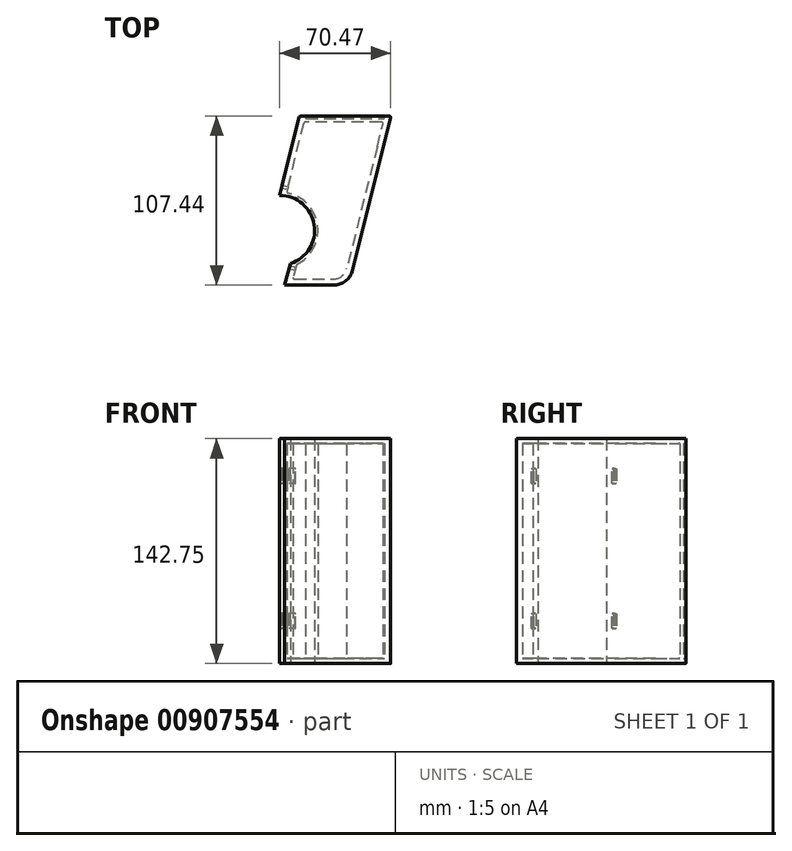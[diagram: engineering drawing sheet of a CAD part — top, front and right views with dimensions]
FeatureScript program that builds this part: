
annotation { "Feature Type Name" : "Feature", "Feature Type Description" : "" }
export const myFeature = defineFeature(function(context is Context, id is Id, definition is map)
    precondition{}
    {
        {
            var Q0;
            Q0=qCreatedBy(makeId("Top.planeOp"),FACE);
            var sketch = newSketch(context, id + "F0", { "sketchPlane" : qUnion([Q0])});
            skArc(sketch, "E0", {"start": v(6.82, -21.15) * mm, "mid": v(21.96, 3.45) * mm, "end": v(0, 22.23) * mm});
            skLineSegment(sketch, "E1", {"start": v(0, 22.22) * mm, "end": v(1.58, 28.53) * mm});
            skLineSegment(sketch, "E2.trimOffspring", {"start": v(6.82, -21.15) * mm, "end": v(3.22, -34.85) * mm});
            skLineSegment(sketch, "E3", {"start": v(3.22, -34.85) * mm, "end": v(16.42, -34.85) * mm});
            skPoint(sketch, "E4.orphan", {"position": v(0, -47.1) * mm});
            skPoint(sketch, "E5.visualSharp", {"position": v(36.5, -34.85) * mm});
            skPoint(sketch, "E6.newPointB", {"position": v(49.9, -44.72) * mm});
            skLineSegment(sketch, "E7", {"start": v(3.22, -34.85) * mm, "end": v(0.71, -44.38) * mm});
            skLineSegment(sketch, "E8", {"start": v(0.71, -44.38) * mm, "end": v(16.4, -44.38) * mm});
            skLineSegment(sketch, "E9.0", {"start": v(66.86, 57.06) * mm, "end": v(48.28, -17.24) * mm});
            skLineSegment(sketch, "E10", {"start": v(16.42, -34.85) * mm, "end": v(33.97, -34.85) * mm});
            skLineSegment(sketch, "E11", {"start": v(1.58, 28.53) * mm, "end": v(8.82, 57.52) * mm});
            skArc(sketch, "E12.filletArc", {"start": v(33.97, -34.85) * mm, "mid": v(41.73, -32.2) * mm, "end": v(46.26, -25.35) * mm});
            skLineSegment(sketch, "E13", {"start": v(48.28, -17.24) * mm, "end": v(46.26, -25.35) * mm});
            skLineSegment(sketch, "E14.0", {"start": v(9.88, -24.5) * mm, "end": v(8.48, -29.83) * mm});
            skLineSegment(sketch, "E14.1", {"start": v(9.41, -31.04) * mm, "end": v(16.73, -31.04) * mm});
            skLineSegment(sketch, "E14.2", {"start": v(16.73, -31.04) * mm, "end": v(33.97, -31.04) * mm});
            skArc(sketch, "E14.3", {"start": v(33.97, -31.04) * mm, "mid": v(39.4, -29.19) * mm, "end": v(42.56, -24.4) * mm});
            skLineSegment(sketch, "E14.4", {"start": v(44.59, -16.31) * mm, "end": v(42.56, -24.4) * mm});
            skLineSegment(sketch, "E14.6", {"start": v(5.01, 26.57) * mm, "end": v(5.27, 27.6) * mm});
            skLineSegment(sketch, "E14.7", {"start": v(5.27, 27.6) * mm, "end": v(11.8, 53.7) * mm});
            skLineSegment(sketch, "E14.10", {"start": v(61.97, 53.23) * mm, "end": v(44.59, -16.31) * mm});
            skPoint(sketch, "E15.visualSharp", {"position": v(4.77, 25.6) * mm});
            skPoint(sketch, "E16.visualSharp", {"position": v(8.16, -31.04) * mm});
            skArc(sketch, "E16.filletArc", {"start": v(8.48, -29.83) * mm, "mid": v(8.65, -30.66) * mm, "end": v(9.41, -31.04) * mm});
            skPoint(sketch, "E17.visualSharp", {"position": v(10, -24.04) * mm});
            skArc(sketch, "E18.0", {"start": v(10.68, -21.78) * mm, "mid": v(24.09, 2.85) * mm, "end": v(5.3, 23.67) * mm});
            skLineSegment(sketch, "E19", {"start": v(9.88, -24.5) * mm, "end": v(10.55, -21.93) * mm});
            skArc(sketch, "E20.filletArc", {"start": v(10.68, -21.78) * mm, "mid": v(10.6, -21.84) * mm, "end": v(10.55, -21.93) * mm});
            skLineSegment(sketch, "E21", {"start": v(5.01, 26.57) * mm, "end": v(4.58, 24.85) * mm});
            skArc(sketch, "E22.filletArc", {"start": v(4.58, 24.85) * mm, "mid": v(4.7, 24.1) * mm, "end": v(5.3, 23.67) * mm});
            skLineSegment(sketch, "E23.0", {"start": v(16.3, 72.6) * mm, "end": v(13.35, 72.6) * mm});
            skLineSegment(sketch, "E24", {"start": v(66.86, 57.06) * mm, "end": v(70.44, 71.4) * mm});
            skLineSegment(sketch, "E25", {"start": v(8.82, 57.52) * mm, "end": v(12.4, 71.86) * mm});
            skLineSegment(sketch, "E26", {"start": v(66.66, 72.6) * mm, "end": v(69.5, 72.6) * mm});
            skArc(sketch, "E27.filletArc", {"start": v(70.44, 71.4) * mm, "mid": v(70.27, 72.22) * mm, "end": v(69.5, 72.6) * mm});
            skArc(sketch, "E28.filletArc", {"start": v(13.35, 72.6) * mm, "mid": v(12.75, 72.4) * mm, "end": v(12.4, 71.86) * mm});
            skLineSegment(sketch, "E29.0", {"start": v(63, 71.07) * mm, "end": v(16.75, 71.07) * mm});
            skLineSegment(sketch, "E30.0", {"start": v(63, 68.78) * mm, "end": v(16.32, 68.78) * mm});
            skLineSegment(sketch, "E31", {"start": v(11.8, 53.7) * mm, "end": v(15.38, 68.05) * mm});
            skLineSegment(sketch, "E32", {"start": v(61.97, 53.23) * mm, "end": v(65.56, 67.59) * mm});
            skArc(sketch, "E33.filletArc", {"start": v(16.32, 68.78) * mm, "mid": v(15.73, 68.58) * mm, "end": v(15.38, 68.05) * mm});
            skLineSegment(sketch, "E34", {"start": v(63, 68.78) * mm, "end": v(64.63, 68.78) * mm});
            skLineSegment(sketch, "E35", {"start": v(16.52, 72.37) * mm, "end": v(16.52, 71.3) * mm});
            skLineSegment(sketch, "E36", {"start": v(63, 71.07) * mm, "end": v(66.2, 71.07) * mm});
            skLineSegment(sketch, "E37", {"start": v(66.43, 71.3) * mm, "end": v(66.43, 72.37) * mm});
            skPoint(sketch, "E38.newPointA", {"position": v(66.43, 72.6) * mm});
            skArc(sketch, "E38.filletArc", {"start": v(66.66, 72.6) * mm, "mid": v(66.5, 72.53) * mm, "end": v(66.43, 72.37) * mm});
            skPoint(sketch, "E39.visualSharp", {"position": v(66.43, 71.07) * mm});
            skArc(sketch, "E39.filletArc", {"start": v(66.2, 71.07) * mm, "mid": v(66.37, 71.14) * mm, "end": v(66.43, 71.3) * mm});
            skArc(sketch, "E40.filletArc", {"start": v(16.52, 71.3) * mm, "mid": v(16.59, 71.14) * mm, "end": v(16.75, 71.07) * mm});
            skArc(sketch, "E41.filletArc", {"start": v(16.52, 72.37) * mm, "mid": v(16.45, 72.53) * mm, "end": v(16.3, 72.6) * mm});
            skPoint(sketch, "E42.visualSharp", {"position": v(65.86, 68.78) * mm});
            skArc(sketch, "E42.filletArc", {"start": v(65.56, 67.59) * mm, "mid": v(65.39, 68.41) * mm, "end": v(64.63, 68.78) * mm});
            skSolve(sketch);
        }
        {
            var Q0;
            Q0=makeQuery(id+"F0.imprint","IMPRINT",FACE,{"disambiguationData":[TD([[makeQuery(id+"F0.imprint","IMPRINT",EDGE,{"derivedFrom":sQuery(id+"F0.wireOp",EDGE,"E0")}),-1.0]])]});
            extrude(context, id + "F1", {"entities" : qUnion([Q0]), "depth" : 6.35 * mm, "offsetDistance" : 25.4 * mm});
        }
        {
            var Q0;
            Q0 = qSketchRegion(id + "F0", true);
            var Q1;
            Q1=makeQuery(id+"F1.opExtrude","CAP_FACE",FACE,{"disambiguationData":[OSD([sQuery(id+"F0.wireOp",EDGE,"E0"),sQuery(id+"F0.wireOp",EDGE,"E1"),sQuery(id+"F0.wireOp",EDGE,"E2.trimOffspring"),sQuery(id+"F0.wireOp",EDGE,"E3"),sQuery(id+"F0.wireOp",EDGE,"E9.0"),sQuery(id+"F0.wireOp",EDGE,"E10"),sQuery(id+"F0.wireOp",EDGE,"E11"),sQuery(id+"F0.wireOp",EDGE,"UJC1U5ST-MCEr-nF2W-ny8S-TELihmCuxkUr"),sQuery(id+"F0.wireOp",EDGE,"e7e2a3fe-8400-48dc-a1a8-9a47f7191577.filletArc"),sQuery(id+"F0.wireOp",EDGE,"f4f465a5-f153-4e84-8156-ec9705fb6cea.filletArc"),sQuery(id+"F0.wireOp",EDGE,"E12.filletArc"),sQuery(id+"F0.wireOp",EDGE,"E13"),sQuery(id+"F0.wireOp",EDGE,"E14.0"),sQuery(id+"F0.wireOp",EDGE,"E14.1"),sQuery(id+"F0.wireOp",EDGE,"E14.2"),sQuery(id+"F0.wireOp",EDGE,"E14.3"),sQuery(id+"F0.wireOp",EDGE,"E14.4"),sQuery(id+"F0.wireOp",EDGE,"E14.5"),sQuery(id+"F0.wireOp",EDGE,"E14.6"),sQuery(id+"F0.wireOp",EDGE,"E14.7"),sQuery(id+"F0.wireOp",EDGE,"E14.8"),sQuery(id+"F0.wireOp",EDGE,"E14.10"),sQuery(id+"F0.wireOp",EDGE,"57333c07-2634-475e-aa19-e25420147b81.filletArc"),sQuery(id+"F0.wireOp",EDGE,"e2d5d6c9-fdbc-41b1-8945-850c04fe5a9c.filletArc"),sQuery(id+"F0.wireOp",EDGE,"E15.filletArc"),sQuery(id+"F0.wireOp",EDGE,"E16.filletArc"),sQuery(id+"F0.wireOp",EDGE,"E17.filletArc")])],"isStart":false});
            extrude(context, id + "F2", {"entities" : qUnion([Q0, Q1]), "operationType" : NewBodyOperationType.ADD, "depth" : 133.35 * mm, "offsetDistance" : 25.4 * mm});
        }
        {
            var Q0;
            {var subQ0=sQuery(id+"F0.wireOp",EDGE,"E2.trimOffspring");Q0=makeQuery(id+"F2.boolean.opBoolean","MERGE",FACE,{"derivedFrom":[makeQuery(id+"F1.opExtrude","SWEPT_FACE",FACE,{"disambiguationData":[OSD([subQ0])]}),makeQuery(id+"F2.opExtrude","SWEPT_FACE",FACE,{"disambiguationData":[OSD([subQ0]),TDD([makeQuery(id+"F0.imprint","IMPRINT",EDGE,{"derivedFrom":subQ0})])]}),makeQuery(id+"F2.opExtrude","SWEPT_FACE",FACE,{"disambiguationData":[OSD([subQ0]),TDD([makeQuery(id+"F1.opExtrude","CAP_EDGE",EDGE,{"disambiguationData":[OSD([subQ0])],"isStart":false})])]})]});}
            var sketch = newSketch(context, id + "F3", { "sketchPlane" : qUnion([Q0])});
            skLineSegment(sketch, "E43.0", {"start": v(20.56, 19.05) * mm, "end": v(21.97, 19.05) * mm});
            skLineSegment(sketch, "E44.0", {"start": v(20.56, 120.65) * mm, "end": v(21.97, 120.65) * mm});
            skLineSegment(sketch, "E45.0", {"start": v(20.31, 120.4) * mm, "end": v(20.31, 111.37) * mm});
            skLineSegment(sketch, "E46.0", {"start": v(22.22, 120.4) * mm, "end": v(22.22, 111.37) * mm});
            skLineSegment(sketch, "E47.0", {"start": v(20.57, 28.58) * mm, "end": v(21.97, 28.58) * mm});
            skLineSegment(sketch, "E48.0", {"start": v(20.56, 111.13) * mm, "end": v(21.97, 111.13) * mm});
            skLineSegment(sketch, "E49.trimOffspring", {"start": v(22.22, 28.33) * mm, "end": v(22.22, 19.3) * mm});
            skLineSegment(sketch, "E50.trimOffspring", {"start": v(20.31, 28.32) * mm, "end": v(20.31, 19.3) * mm});
            skPoint(sketch, "E51.visualSharp", {"position": v(20.31, 28.58) * mm});
            skArc(sketch, "E51.filletArc", {"start": v(20.57, 28.58) * mm, "mid": v(20.39, 28.5) * mm, "end": v(20.31, 28.32) * mm});
            skPoint(sketch, "E52.visualSharp", {"position": v(22.22, 28.58) * mm});
            skArc(sketch, "E52.filletArc", {"start": v(22.22, 28.33) * mm, "mid": v(22.14, 28.5) * mm, "end": v(21.97, 28.57) * mm});
            skPoint(sketch, "E53.visualSharp", {"position": v(22.22, 19.05) * mm});
            skArc(sketch, "E53.filletArc", {"start": v(21.97, 19.05) * mm, "mid": v(22.14, 19.12) * mm, "end": v(22.22, 19.3) * mm});
            skPoint(sketch, "E54.visualSharp", {"position": v(20.31, 19.05) * mm});
            skArc(sketch, "E54.filletArc", {"start": v(20.31, 19.3) * mm, "mid": v(20.38, 19.12) * mm, "end": v(20.56, 19.05) * mm});
            skPoint(sketch, "E55.visualSharp", {"position": v(20.31, 120.65) * mm});
            skArc(sketch, "E55.filletArc", {"start": v(20.56, 120.65) * mm, "mid": v(20.38, 120.58) * mm, "end": v(20.31, 120.4) * mm});
            skPoint(sketch, "E56.visualSharp", {"position": v(20.31, 111.13) * mm});
            skArc(sketch, "E56.filletArc", {"start": v(20.31, 111.37) * mm, "mid": v(20.38, 111.2) * mm, "end": v(20.56, 111.13) * mm});
            skPoint(sketch, "E57.visualSharp", {"position": v(22.22, 120.65) * mm});
            skArc(sketch, "E57.filletArc", {"start": v(22.22, 120.4) * mm, "mid": v(22.14, 120.58) * mm, "end": v(21.97, 120.65) * mm});
            skPoint(sketch, "E58.visualSharp", {"position": v(22.22, 111.13) * mm});
            skArc(sketch, "E58.filletArc", {"start": v(21.97, 111.13) * mm, "mid": v(22.14, 111.2) * mm, "end": v(22.22, 111.37) * mm});
            skSolve(sketch);
        }
        {
            var Q0;
            Q0=makeQuery(id+"F3.imprint","IMPRINT",FACE,{"disambiguationData":[TD([[makeQuery(id+"F3.imprint","IMPRINT",EDGE,{"derivedFrom":sQuery(id+"F3.wireOp",EDGE,"E43.0")}),1.0]])]});
            var Q1;
            Q1=makeQuery(id+"F3.imprint","IMPRINT",FACE,{"disambiguationData":[TD([[makeQuery(id+"F3.imprint","IMPRINT",EDGE,{"derivedFrom":sQuery(id+"F3.wireOp",EDGE,"E44.0")}),-1.0]])]});
            extrude(context, id + "F4", {"entities" : qUnion([Q0, Q1]), "operationType" : NewBodyOperationType.REMOVE, "oppositeDirection" : true, "depth" : 12.7 * mm, "offsetDistance" : 25.4 * mm});
        }
        {
            var Q0;
            {var subQ0=sQuery(id+"F0.wireOp",EDGE,"E1");Q0=makeQuery(id+"F2.boolean.opBoolean","MERGE",FACE,{"derivedFrom":[makeQuery(id+"F1.opExtrude","SWEPT_FACE",FACE,{"disambiguationData":[OSD([subQ0])]}),makeQuery(id+"F2.opExtrude","SWEPT_FACE",FACE,{"disambiguationData":[OSD([subQ0]),TDD([makeQuery(id+"F0.imprint","IMPRINT",EDGE,{"derivedFrom":subQ0})])]}),makeQuery(id+"F2.opExtrude","SWEPT_FACE",FACE,{"disambiguationData":[OSD([subQ0]),TDD([makeQuery(id+"F1.opExtrude","CAP_EDGE",EDGE,{"disambiguationData":[OSD([subQ0])],"isStart":false})])]})]});}
            var sketch = newSketch(context, id + "F5", { "sketchPlane" : qUnion([Q0])});
            skLineSegment(sketch, "E59.0", {"start": v(-26.16, 120.4) * mm, "end": v(-26.16, 111.37) * mm});
            skLineSegment(sketch, "E60.0", {"start": v(-26.4, 19.05) * mm, "end": v(-27.81, 19.05) * mm});
            skLineSegment(sketch, "E61.0", {"start": v(-26.4, 120.65) * mm, "end": v(-27.81, 120.65) * mm});
            skLineSegment(sketch, "E62.0", {"start": v(-26.4, 111.13) * mm, "end": v(-27.81, 111.13) * mm});
            skLineSegment(sketch, "E63.0", {"start": v(-26.4, 28.58) * mm, "end": v(-27.81, 28.58) * mm});
            skLineSegment(sketch, "E64", {"start": v(-28.06, 28.33) * mm, "end": v(-28.06, 19.3) * mm});
            skLineSegment(sketch, "E65", {"start": v(-28.06, 120.4) * mm, "end": v(-28.06, 111.37) * mm});
            skArc(sketch, "E66.filletArc", {"start": v(-26.16, 120.4) * mm, "mid": v(-26.23, 120.58) * mm, "end": v(-26.4, 120.65) * mm});
            skArc(sketch, "E67.filletArc", {"start": v(-26.4, 111.13) * mm, "mid": v(-26.23, 111.2) * mm, "end": v(-26.16, 111.37) * mm});
            skPoint(sketch, "E68.visualSharp", {"position": v(-28.06, 111.13) * mm});
            skArc(sketch, "E68.filletArc", {"start": v(-28.06, 111.37) * mm, "mid": v(-27.99, 111.2) * mm, "end": v(-27.81, 111.12) * mm});
            skPoint(sketch, "E69.visualSharp", {"position": v(-28.06, 120.65) * mm});
            skArc(sketch, "E69.filletArc", {"start": v(-27.81, 120.65) * mm, "mid": v(-27.99, 120.58) * mm, "end": v(-28.06, 120.4) * mm});
            skLineSegment(sketch, "E70.0", {"start": v(-26.16, 28.33) * mm, "end": v(-26.16, 19.3) * mm});
            skPoint(sketch, "E71.visualSharp", {"position": v(-28.06, 28.58) * mm});
            skArc(sketch, "E71.filletArc", {"start": v(-27.81, 28.58) * mm, "mid": v(-27.99, 28.5) * mm, "end": v(-28.06, 28.33) * mm});
            skPoint(sketch, "E72.visualSharp", {"position": v(-28.06, 19.05) * mm});
            skArc(sketch, "E72.filletArc", {"start": v(-28.06, 19.3) * mm, "mid": v(-27.99, 19.12) * mm, "end": v(-27.81, 19.05) * mm});
            skArc(sketch, "E73.filletArc", {"start": v(-26.4, 19.05) * mm, "mid": v(-26.23, 19.12) * mm, "end": v(-26.16, 19.3) * mm});
            skArc(sketch, "E74.filletArc", {"start": v(-26.16, 28.33) * mm, "mid": v(-26.23, 28.5) * mm, "end": v(-26.4, 28.58) * mm});
            skSolve(sketch);
        }
        {
            var Q0;
            Q0=makeQuery(id+"F5.imprint","IMPRINT",FACE,{"disambiguationData":[TD([[makeQuery(id+"F5.imprint","IMPRINT",EDGE,{"derivedFrom":sQuery(id+"F5.wireOp",EDGE,"E59.0")}),-1.0]])]});
            var Q1;
            Q1=makeQuery(id+"F5.imprint","IMPRINT",FACE,{"disambiguationData":[TD([[makeQuery(id+"F5.imprint","IMPRINT",EDGE,{"derivedFrom":sQuery(id+"F5.wireOp",EDGE,"E60.0")}),-1.0]])]});
            extrude(context, id + "F6", {"entities" : qUnion([Q0, Q1]), "operationType" : NewBodyOperationType.REMOVE, "oppositeDirection" : true, "depth" : 12.7 * mm, "offsetDistance" : 25.4 * mm});
        }
        {
            var Q0;
            Q0=qCreatedBy(makeId("Top.planeOp"),FACE);
            var sketch = newSketch(context, id + "F7", { "sketchPlane" : qUnion([Q0])});
            skLineSegment(sketch, "E75.0", {"start": v(3.22, -34.85) * mm, "end": v(33.97, -34.85) * mm});
            skArc(sketch, "E76.0", {"start": v(33.97, -34.85) * mm, "mid": v(41.73, -32.2) * mm, "end": v(46.26, -25.35) * mm});
            skLineSegment(sketch, "E77.0", {"start": v(66.86, 57.06) * mm, "end": v(46.26, -25.35) * mm});
            skLineSegment(sketch, "E78.0", {"start": v(1.58, 28.53) * mm, "end": v(1.58, 28.53) * mm});
            skLineSegment(sketch, "E79.0", {"start": v(0, 22.22) * mm, "end": v(1.58, 28.53) * mm});
            skArc(sketch, "E80.0", {"start": v(6.82, -21.15) * mm, "mid": v(21.96, 3.45) * mm, "end": v(0, 22.22) * mm});
            skPoint(sketch, "E81.0", {"position": v(6.35, -22.93) * mm});
            skPoint(sketch, "E82.0", {"position": v(5.02, -28) * mm});
            skPoint(sketch, "E83.0", {"position": v(6, -24.29) * mm});
            skPoint(sketch, "E84.0", {"position": v(6.82, -21.15) * mm});
            skPoint(sketch, "E85.0", {"position": v(3.22, -34.85) * mm});
            skLineSegment(sketch, "E86.0", {"start": v(6.82, -21.15) * mm, "end": v(3.22, -34.85) * mm});
            skLineSegment(sketch, "E87.0", {"start": v(1.58, 28.53) * mm, "end": v(12.4, 71.86) * mm});
            skPoint(sketch, "E88.0", {"position": v(1.11, 26.68) * mm});
            skArc(sketch, "E89.0.0", {"start": v(66.2, 71.07) * mm, "mid": v(66.37, 71.14) * mm, "end": v(66.43, 71.3) * mm});
            skLineSegment(sketch, "E89.0.1", {"start": v(66.43, 71.3) * mm, "end": v(66.43, 72.37) * mm});
            skArc(sketch, "E89.0.2", {"start": v(66.43, 72.37) * mm, "mid": v(66.5, 72.53) * mm, "end": v(66.66, 72.6) * mm});
            skLineSegment(sketch, "E89.0.3", {"start": v(66.66, 72.6) * mm, "end": v(69.5, 72.6) * mm});
            skArc(sketch, "E89.0.4", {"start": v(69.5, 72.6) * mm, "mid": v(70.27, 72.22) * mm, "end": v(70.44, 71.4) * mm});
            skLineSegment(sketch, "E89.0.5", {"start": v(70.44, 71.4) * mm, "end": v(46.26, -25.35) * mm});
            skArc(sketch, "E89.0.6", {"start": v(46.26, -25.35) * mm, "mid": v(41.73, -32.2) * mm, "end": v(33.97, -34.85) * mm});
            skLineSegment(sketch, "E89.0.7", {"start": v(33.97, -34.85) * mm, "end": v(3.22, -34.85) * mm});
            skLineSegment(sketch, "E89.0.8", {"start": v(3.22, -34.85) * mm, "end": v(6.82, -21.15) * mm});
            skArc(sketch, "E89.0.12", {"start": v(12.4, 71.86) * mm, "mid": v(12.75, 72.4) * mm, "end": v(13.35, 72.6) * mm});
            skLineSegment(sketch, "E89.0.13", {"start": v(13.35, 72.6) * mm, "end": v(16.3, 72.6) * mm});
            skArc(sketch, "E89.0.14", {"start": v(16.3, 72.6) * mm, "mid": v(16.45, 72.53) * mm, "end": v(16.52, 72.37) * mm});
            skLineSegment(sketch, "E89.0.15", {"start": v(16.52, 72.37) * mm, "end": v(16.52, 71.3) * mm});
            skArc(sketch, "E89.0.16", {"start": v(16.52, 71.3) * mm, "mid": v(16.59, 71.14) * mm, "end": v(16.75, 71.07) * mm});
            skLineSegment(sketch, "E89.0.17", {"start": v(16.75, 71.07) * mm, "end": v(66.2, 71.07) * mm});
            skLineSegment(sketch, "E90", {"start": v(16.3, 72.6) * mm, "end": v(66.66, 72.6) * mm});
            skSolve(sketch);
        }
        {
            var Q0;
            {var subQ0=sQuery(id+"F0.wireOp",EDGE,"E22.filletArc");var subQ1=sQuery(id+"F0.wireOp",EDGE,"E21");var subQ2=sQuery(id+"F0.wireOp",EDGE,"E20.filletArc");var subQ3=sQuery(id+"F0.wireOp",EDGE,"E19");var subQ4=sQuery(id+"F0.wireOp",EDGE,"E18.0");var subQ5=sQuery(id+"F0.wireOp",EDGE,"31bc3a16-06b6-44d1-a6b1-977c0b372265.filletArc");var subQ6=sQuery(id+"F0.wireOp",EDGE,"0de4bd6d-7a91-43b7-a1aa-ad65d0cba0ae.filletArc");var subQ7=sQuery(id+"F0.wireOp",EDGE,"b0323423-f888-4abb-9b28-227df9114c8d.filletArc");var subQ8=sQuery(id+"F0.wireOp",EDGE,"c9f2cd7f-757e-4f4c-9d55-a754993df767.filletArc");var subQ9=sQuery(id+"F0.wireOp",EDGE,"614ea510-6820-4611-a25d-42c91d798e97.trimOffspring");var subQ10=sQuery(id+"F0.wireOp",EDGE,"PRRc91hr-BQM4-kkpM-4t6J-VjuqaAt05xTZ");var subQ11=sQuery(id+"F0.wireOp",EDGE,"7IyvfWwh-164Z-Cb9g-56wf-hmfJlkGNIzxY");var subQ12=sQuery(id+"F0.wireOp",EDGE,"543ce9ba-9488-4f07-bf72-0b5053705f73.0");var subQ13=sQuery(id+"F0.wireOp",EDGE,"E16.filletArc");var subQ14=sQuery(id+"F0.wireOp",EDGE,"e2d5d6c9-fdbc-41b1-8945-850c04fe5a9c.filletArc");var subQ15=sQuery(id+"F0.wireOp",EDGE,"57333c07-2634-475e-aa19-e25420147b81.filletArc");var subQ16=sQuery(id+"F0.wireOp",EDGE,"E14.10");var subQ17=sQuery(id+"F0.wireOp",EDGE,"E14.8");var subQ18=sQuery(id+"F0.wireOp",EDGE,"E14.7");var subQ19=sQuery(id+"F0.wireOp",EDGE,"E14.6");var subQ20=sQuery(id+"F0.wireOp",EDGE,"E14.4");var subQ21=sQuery(id+"F0.wireOp",EDGE,"E14.3");var subQ22=sQuery(id+"F0.wireOp",EDGE,"E14.2");var subQ23=sQuery(id+"F0.wireOp",EDGE,"E14.1");var subQ24=sQuery(id+"F0.wireOp",EDGE,"E14.0");var subQ25=sQuery(id+"F0.wireOp",EDGE,"E13");var subQ26=sQuery(id+"F0.wireOp",EDGE,"E12.filletArc");var subQ27=sQuery(id+"F0.wireOp",EDGE,"f4f465a5-f153-4e84-8156-ec9705fb6cea.filletArc");var subQ28=sQuery(id+"F0.wireOp",EDGE,"e7e2a3fe-8400-48dc-a1a8-9a47f7191577.filletArc");var subQ29=sQuery(id+"F0.wireOp",EDGE,"UJC1U5ST-MCEr-nF2W-ny8S-TELihmCuxkUr");var subQ30=sQuery(id+"F0.wireOp",EDGE,"E11");var subQ31=sQuery(id+"F0.wireOp",EDGE,"E10");var subQ32=sQuery(id+"F0.wireOp",EDGE,"E9.0");var subQ33=sQuery(id+"F0.wireOp",EDGE,"E3");var subQ34=sQuery(id+"F0.wireOp",EDGE,"E2.trimOffspring");var subQ35=sQuery(id+"F0.wireOp",EDGE,"E1");var subQ36=sQuery(id+"F0.wireOp",EDGE,"E0");Q0=makeQuery(id+"F2.opExtrude","CAP_FACE",FACE,{"disambiguationData":[OSD([subQ36,subQ35,subQ34,subQ33,subQ32,subQ31,subQ30,subQ29,subQ28,subQ27,subQ26,subQ25,subQ24,subQ23,subQ22,subQ21,subQ20,subQ19,subQ18,subQ17,subQ16,subQ15,subQ14,subQ13,subQ12,subQ11,subQ10,subQ9,subQ8,subQ7,subQ6,subQ5,subQ4,subQ3,subQ2,subQ1,subQ0]),TDD([makeQuery(id+"F1.opExtrude","CAP_FACE",FACE,{"disambiguationData":[OSD([subQ36,subQ35,subQ34,subQ33,subQ32,subQ31,subQ30,subQ29,subQ28,subQ27,subQ26,subQ25,subQ24,subQ23,subQ22,subQ21,subQ20,subQ19,subQ18,subQ17,subQ16,subQ15,subQ14,subQ13,subQ12,subQ11,subQ10,subQ9,subQ8,subQ7,subQ6,subQ5,subQ4,subQ3,subQ2,subQ1,subQ0])],"isStart":false})])],"isStart":false});}
            var sketch = newSketch(context, id + "F8", { "sketchPlane" : qUnion([Q0])});
            skLineSegment(sketch, "E91.0", {"start": v(66.86, 57.06) * mm, "end": v(46.26, -25.35) * mm});
            skLineSegment(sketch, "E92.0.0", {"start": v(46.26, -25.35) * mm, "end": v(66.86, 57.06) * mm});
            skLineSegment(sketch, "E92.0.6", {"start": v(8.82, 57.52) * mm, "end": v(1.58, 28.53) * mm});
            skLineSegment(sketch, "E92.0.7", {"start": v(1.58, 28.53) * mm, "end": v(0, 22.22) * mm});
            skArc(sketch, "E92.0.8", {"start": v(0, 22.23) * mm, "mid": v(21.96, 3.45) * mm, "end": v(6.82, -21.15) * mm});
            skLineSegment(sketch, "E92.0.9", {"start": v(6.82, -21.15) * mm, "end": v(3.22, -34.85) * mm});
            skLineSegment(sketch, "E92.0.10", {"start": v(3.22, -34.85) * mm, "end": v(33.97, -34.85) * mm});
            skArc(sketch, "E92.0.11", {"start": v(33.97, -34.85) * mm, "mid": v(41.73, -32.2) * mm, "end": v(46.26, -25.35) * mm});
            skPoint(sketch, "E93.0", {"position": v(16.3, 72.6) * mm});
            skPoint(sketch, "E94.0", {"position": v(66.66, 72.6) * mm});
            skLineSegment(sketch, "E95.0", {"start": v(1.58, 28.53) * mm, "end": v(12.4, 71.86) * mm});
            skLineSegment(sketch, "E96.0", {"start": v(16.3, 72.6) * mm, "end": v(13.35, 72.6) * mm});
            skPoint(sketch, "E97.0", {"position": v(12.75, 72.4) * mm});
            skLineSegment(sketch, "E98.0", {"start": v(66.66, 72.6) * mm, "end": v(69.5, 72.6) * mm});
            skPoint(sketch, "E99.0", {"position": v(70.27, 72.22) * mm});
            skArc(sketch, "E100.0", {"start": v(70.44, 71.4) * mm, "mid": v(70.27, 72.22) * mm, "end": v(69.5, 72.6) * mm});
            skLineSegment(sketch, "E101.0", {"start": v(70.44, 71.4) * mm, "end": v(46.26, -25.35) * mm});
            skArc(sketch, "E102.0.0", {"start": v(66.43, 71.3) * mm, "mid": v(66.37, 71.14) * mm, "end": v(66.2, 71.07) * mm});
            skLineSegment(sketch, "E102.0.1", {"start": v(66.2, 71.07) * mm, "end": v(16.75, 71.07) * mm});
            skArc(sketch, "E102.0.2", {"start": v(16.75, 71.07) * mm, "mid": v(16.59, 71.14) * mm, "end": v(16.52, 71.3) * mm});
            skLineSegment(sketch, "E102.0.3", {"start": v(16.52, 71.3) * mm, "end": v(16.52, 72.37) * mm});
            skArc(sketch, "E102.0.4", {"start": v(16.52, 72.37) * mm, "mid": v(16.45, 72.53) * mm, "end": v(16.3, 72.6) * mm});
            skArc(sketch, "E102.0.6", {"start": v(13.35, 72.6) * mm, "mid": v(12.75, 72.4) * mm, "end": v(12.4, 71.86) * mm});
            skLineSegment(sketch, "E102.0.7", {"start": v(12.4, 71.86) * mm, "end": v(1.58, 28.53) * mm});
            skArc(sketch, "E102.0.9", {"start": v(0, 22.22) * mm, "mid": v(21.96, 3.45) * mm, "end": v(6.82, -21.15) * mm});
            skLineSegment(sketch, "E102.0.13", {"start": v(46.26, -25.35) * mm, "end": v(70.44, 71.4) * mm});
            skLineSegment(sketch, "E102.0.15", {"start": v(69.5, 72.6) * mm, "end": v(66.66, 72.6) * mm});
            skArc(sketch, "E102.0.16", {"start": v(66.66, 72.6) * mm, "mid": v(66.5, 72.53) * mm, "end": v(66.43, 72.37) * mm});
            skLineSegment(sketch, "E102.0.17", {"start": v(66.43, 72.37) * mm, "end": v(66.43, 71.3) * mm});
            skLineSegment(sketch, "E103", {"start": v(16.3, 72.6) * mm, "end": v(66.66, 72.6) * mm});
            skSolve(sketch);
        }
        {
            var Q0;
            Q0 = qSketchRegion(id + "F8", true);
            var Q1;
            {var subQ20=sQuery(id+"F0.wireOp",EDGE,"E0");Q1=makeQuery(id+"F8.imprint","IMPRINT",FACE,{"disambiguationData":[TD([[makeQuery(id+"F8.imprint","IMPRINT",EDGE,{"derivedFrom":makeQuery(id+"F2.opExtrude","CAP_EDGE",EDGE,{"disambiguationData":[OSD([subQ20]),TDD([makeQuery(id+"F1.opExtrude","CAP_EDGE",EDGE,{"disambiguationData":[OSD([subQ20])],"isStart":false})])],"isStart":false})}),-1.0]])]});}
            extrude(context, id + "F9", {"entities" : qUnion([Q0, Q1]), "operationType" : NewBodyOperationType.ADD, "oppositeDirection" : true, "depth" : 3.05 * mm, "offsetDistance" : 25.4 * mm});
        }
        {
            var Q0;
            Q0 = qSketchRegion(id + "F7", true);
            extrude(context, id + "F10", {"entities" : qUnion([Q0]), "operationType" : NewBodyOperationType.ADD, "oppositeDirection" : true, "depth" : 3.05 * mm, "offsetDistance" : 25.4 * mm});
        }
    });
